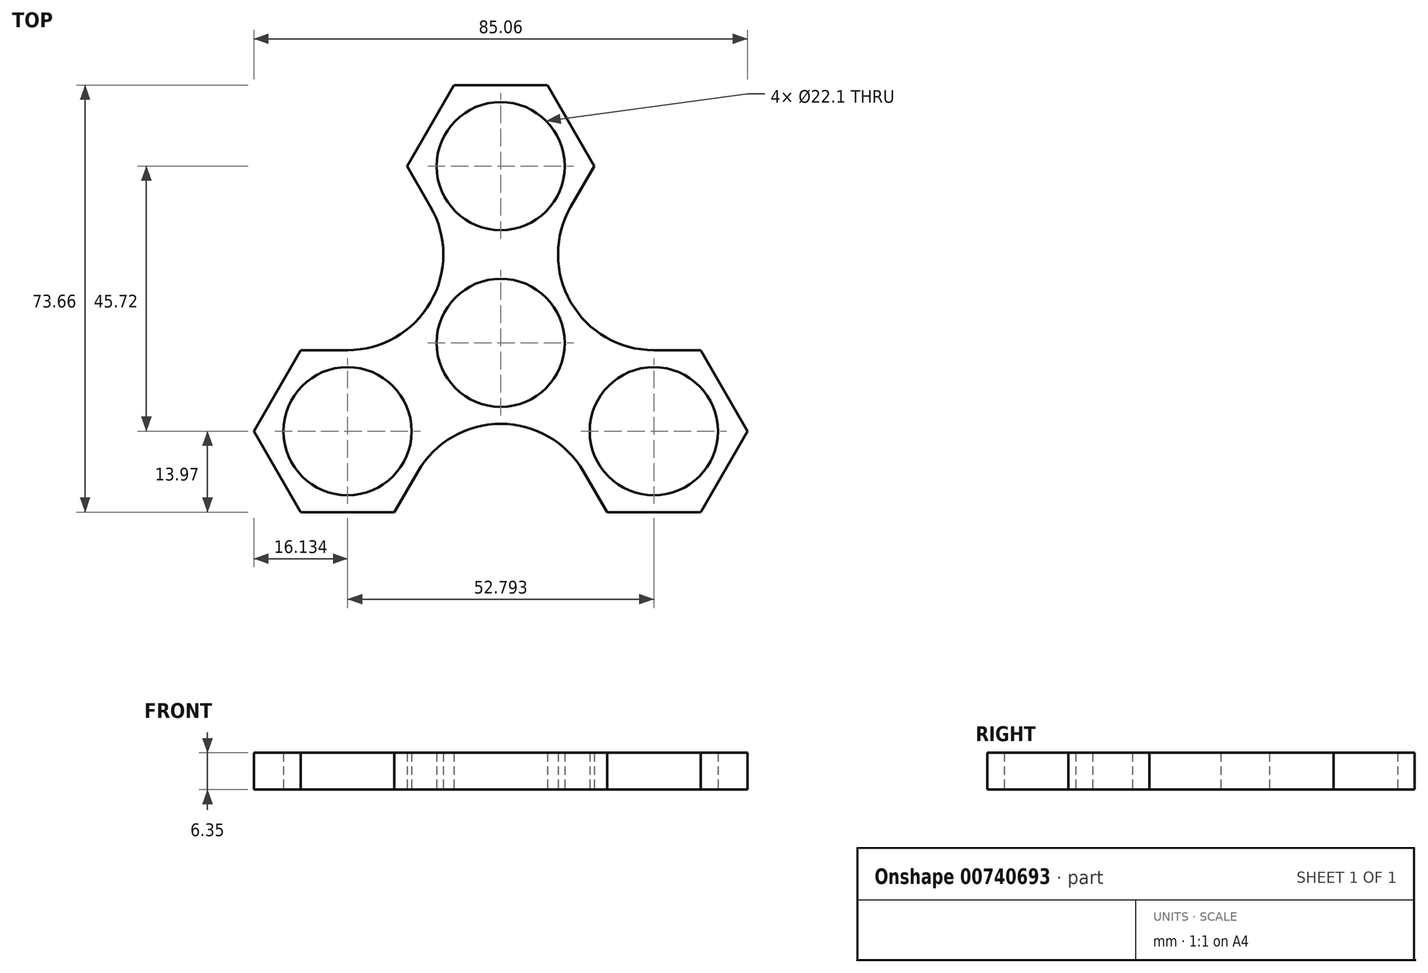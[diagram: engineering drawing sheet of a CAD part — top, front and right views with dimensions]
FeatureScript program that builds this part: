
annotation { "Feature Type Name" : "Feature", "Feature Type Description" : "" }
export const myFeature = defineFeature(function(context is Context, id is Id, definition is map)
    precondition{}
    {
        {
            var Q0;
            Q0=qCreatedBy(makeId("Top.planeOp"),FACE);
            var sketch = newSketch(context, id + "F0", { "sketchPlane" : qUnion([Q0])});
            skCircle(sketch, "E0", {"center": v(0, 0) * mm, "radius": 13.97 * mm});
            skCircle(sketch, "E1", {"center": v(0, 0) * mm, "radius": 11.05 * mm});
            skLineSegment(sketch, "E2", {"start": v(0, 0) * mm, "end": v(0, 30.48) * mm});
            skCircle(sketch, "E3", {"center": v(0, 30.48) * mm, "radius": 11.05 * mm});
            skCircle(sketch, "E4", {"center": v(0, 30.48) * mm, "radius": 13.97 * mm});
            skLineSegment(sketch, "E5.1.0", {"start": v(0, 0) * mm, "end": v(-26.4, -15.24) * mm});
            skCircle(sketch, "E5.1.1", {"center": v(-26.4, -15.24) * mm, "radius": 11.05 * mm});
            skLineSegment(sketch, "E5.2.0", {"start": v(0, 0) * mm, "end": v(26.4, -15.24) * mm});
            skCircle(sketch, "E5.2.1", {"center": v(26.4, -15.24) * mm, "radius": 11.05 * mm});
            skCircle(sketch, "E6.1.1", {"center": v(-26.4, -15.24) * mm, "radius": 13.97 * mm});
            skCircle(sketch, "E6.2.1", {"center": v(26.4, -15.24) * mm, "radius": 13.97 * mm});
            skLineSegment(sketch, "E7", {"start": v(0, 0) * mm, "end": v(0, -30.48) * mm});
            skArc(sketch, "E8", {"start": v(14.3, -22.23) * mm, "mid": v(0, -13.97) * mm, "end": v(-14.3, -22.23) * mm});
            skArc(sketch, "E9.1.0", {"start": v(12.1, 23.5) * mm, "mid": v(12.1, 6.99) * mm, "end": v(26.4, -1.27) * mm});
            skArc(sketch, "E9.2.0", {"start": v(-26.4, -1.27) * mm, "mid": v(-12.1, 6.99) * mm, "end": v(-12.1, 23.5) * mm});
            skPoint(sketch, "E10", {"position": v(26.4, -29.21) * mm});
            skPoint(sketch, "E11", {"position": v(40.37, -15.24) * mm});
            skCircle(sketch, "E12.cCircle", {"center": v(-26.4, -15.24) * mm, "radius": 13.97 * mm, "construction": true});
            skLineSegment(sketch, "E12.0", {"start": v(-10.27, -15.24) * mm, "end": v(-18.33, -29.21) * mm});
            skLineSegment(sketch, "E12.1", {"start": v(-18.33, -29.21) * mm, "end": v(-34.46, -29.21) * mm});
            skLineSegment(sketch, "E12.2", {"start": v(-34.46, -29.21) * mm, "end": v(-42.53, -15.24) * mm});
            skLineSegment(sketch, "E12.3", {"start": v(-42.53, -15.24) * mm, "end": v(-34.46, -1.27) * mm});
            skLineSegment(sketch, "E12.4", {"start": v(-34.46, -1.27) * mm, "end": v(-18.33, -1.27) * mm});
            skLineSegment(sketch, "E12.5", {"start": v(-18.33, -1.27) * mm, "end": v(-10.27, -15.24) * mm});
            skPoint(sketch, "E12.0.midPoint", {"position": v(-14.3, -22.23) * mm});
            skCircle(sketch, "E13.1.0", {"center": v(26.4, -15.24) * mm, "radius": 13.97 * mm, "construction": true});
            skCircle(sketch, "E13.2.0", {"center": v(0, 30.48) * mm, "radius": 13.97 * mm, "construction": true});
            skLineSegment(sketch, "E14.0", {"start": v(16.13, 30.48) * mm, "end": v(8.07, 16.5) * mm});
            skLineSegment(sketch, "E14.1", {"start": v(8.07, 16.5) * mm, "end": v(-8.07, 16.5) * mm});
            skLineSegment(sketch, "E14.2", {"start": v(-8.07, 16.5) * mm, "end": v(-16.13, 30.48) * mm});
            skLineSegment(sketch, "E14.3", {"start": v(-16.13, 30.48) * mm, "end": v(-8.07, 44.45) * mm});
            skLineSegment(sketch, "E14.4", {"start": v(-8.07, 44.45) * mm, "end": v(8.07, 44.45) * mm});
            skLineSegment(sketch, "E14.5", {"start": v(8.07, 44.45) * mm, "end": v(16.13, 30.48) * mm});
            skPoint(sketch, "E14.0.midPoint", {"position": v(12.1, 23.5) * mm});
            skLineSegment(sketch, "E15.0", {"start": v(42.53, -15.24) * mm, "end": v(34.46, -29.21) * mm});
            skLineSegment(sketch, "E15.1", {"start": v(34.46, -29.21) * mm, "end": v(18.33, -29.21) * mm});
            skLineSegment(sketch, "E15.2", {"start": v(18.33, -29.21) * mm, "end": v(10.27, -15.24) * mm});
            skLineSegment(sketch, "E15.3", {"start": v(10.27, -15.24) * mm, "end": v(18.33, -1.27) * mm});
            skLineSegment(sketch, "E15.4", {"start": v(18.33, -1.27) * mm, "end": v(34.46, -1.27) * mm});
            skLineSegment(sketch, "E15.5", {"start": v(34.46, -1.27) * mm, "end": v(42.53, -15.24) * mm});
            skPoint(sketch, "E15.0.midPoint", {"position": v(38.5, -22.23) * mm});
            skSolve(sketch);
        }
        {
            var Q0;
            Q0 = qSketchRegion(id + "F0", true);
            extrude(context, id + "F1", {"entities" : qUnion([Q0]), "depth" : 6.35 * mm, "offsetDistance" : 25.4 * mm});
        }
    });
